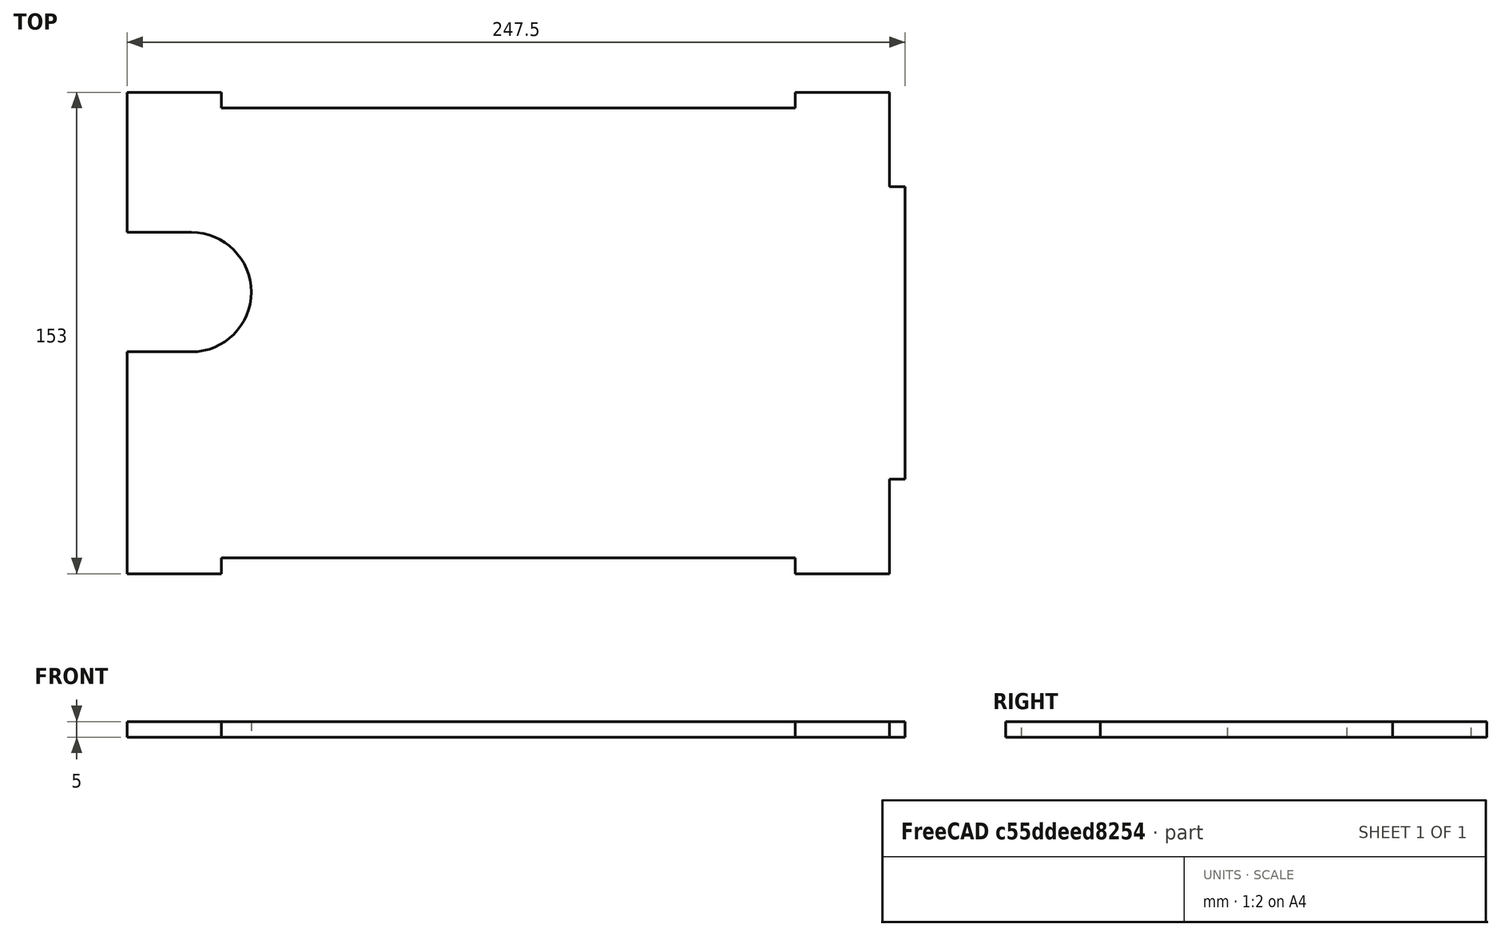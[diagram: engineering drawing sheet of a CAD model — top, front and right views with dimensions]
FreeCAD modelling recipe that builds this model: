
FCSTD DOCUMENT  (FreeCAD 0.15R4671 (Git))
Label: lower_side_axis_B
License: All rights reserved
LicenseURL: http://en.wikipedia.org/wiki/All_rights_reserved
objects: Sketcher::SketchObject×1, PartDesign::Pad×1
note: 3 computed .brp shape members not serialized (recipe doc carries the construction recipe); baked Part::Feature solids carry a one-line shape summary decoded from their .brp

FEATURE [Sketcher::SketchObject] Sketch
  sketch-geometry (20):
    g0: LineSegment StartX=121.25 StartY=46.5 StartZ=0 EndX=121.25 EndY=76.5 EndZ=0
    g1: LineSegment StartX=121.25 StartY=76.5 StartZ=0 EndX=91.25 EndY=76.5 EndZ=0
    g2: LineSegment StartX=91.25 StartY=76.5 StartZ=0 EndX=91.25 EndY=71.5 EndZ=0
    g3: LineSegment StartX=91.25 StartY=71.5 StartZ=0 EndX=-91.25 EndY=71.5 EndZ=0
    g4: LineSegment StartX=-91.25 StartY=71.5 StartZ=0 EndX=-91.25 EndY=76.5 EndZ=0
    g5: LineSegment StartX=-91.25 StartY=76.5 StartZ=0 EndX=-121.25 EndY=76.5 EndZ=0
    g6: LineSegment StartX=-121.25 StartY=76.5 StartZ=0 EndX=-121.25 EndY=32 EndZ=0
    g7: LineSegment StartX=-121.25 StartY=-6 StartZ=0 EndX=-121.25 EndY=-76.5 EndZ=0
    g8: LineSegment StartX=-121.25 StartY=-76.5 StartZ=0 EndX=-91.25 EndY=-76.5 EndZ=0
    g9: LineSegment StartX=-91.25 StartY=-76.5 StartZ=0 EndX=-91.25 EndY=-71.5 EndZ=0
    g10: LineSegment StartX=-91.25 StartY=-71.5 StartZ=0 EndX=91.25 EndY=-71.5 EndZ=0
    g11: LineSegment StartX=91.25 StartY=-71.5 StartZ=0 EndX=91.25 EndY=-76.5 EndZ=0
    g12: LineSegment StartX=91.25 StartY=-76.5 StartZ=0 EndX=121.25 EndY=-76.5 EndZ=0
    g13: LineSegment StartX=121.25 StartY=-76.5 StartZ=0 EndX=121.25 EndY=-46.5 EndZ=0
    g14: LineSegment StartX=121.25 StartY=-46.5 StartZ=0 EndX=126.25 EndY=-46.5 EndZ=0
    g15: LineSegment StartX=126.25 StartY=-46.5 StartZ=0 EndX=126.25 EndY=46.5 EndZ=0
    g16: LineSegment StartX=126.25 StartY=46.5 StartZ=0 EndX=121.25 EndY=46.5 EndZ=0
    g17: LineSegment StartX=-121.25 StartY=32 StartZ=0 EndX=-100.75 EndY=32 EndZ=0
    g18: ArcOfCircle CenterX=-100.75 CenterY=13 CenterZ=0 NormalX=0 NormalY=0 NormalZ=1 Radius=19 StartAngle=4.71239 EndAngle=7.85398
    g19: LineSegment StartX=-100.75 StartY=-6 StartZ=0 EndX=-121.25 EndY=-6 EndZ=0
  constraints (59):
    c: Coincident(g5,g6)
    c: Coincident(g4,g5)
    c: Coincident(g3,g4)
    c: Coincident(g2,g3)
    c: Coincident(g1,g2)
    c: Coincident(g0,g1)
    c: Coincident(g0,g16)
    c: Coincident(g15,g16)
    c: Coincident(g14,g15)
    c: Coincident(g13,g14)
    c: Coincident(g12,g13)
    c: Coincident(g11,g12)
    c: Coincident(g10,g11)
    c: Coincident(g9,g10)
    c: Coincident(g8,g9)
    c: Coincident(g7,g8)
    c: Vertical(g6)
    c: Vertical(g7)
    c: Vertical(g9)
    c: Vertical(g4)
    c: Vertical(g2)
    c: Vertical(g11)
    c: Vertical(g13)
    c: Vertical(g15)
    c: Vertical(g0)
    c: Horizontal(g5)
    c: Horizontal(g3)
    c: Horizontal(g1)
    c: Horizontal(g16)
    c: Horizontal(g14)
    c: Horizontal(g12)
    c: Horizontal(g10)
    c: Horizontal(g8)
    c: Equal(g4,g2)
    c: Equal(g2,g16)
    c: Equal(g16,g14)
    c: Equal(g14,g11)
    c: Equal(g11,g9)
    c: DistanceX(g16) = -5
    c: Equal(g5,g1)
    c: Equal(g1,g0)
    c: Equal(g0,g13)
    c: Equal(g13,g12)
    c: Equal(g12,g8)
    c: DistanceX(g1) = -30
    c: DistanceX(g5,g0) = 242.5
    c: DistanceY(g3,g9) = -143
    c: Coincident(g6,g17)
    c: Horizontal(g17)
    c: Tangent(g17,g18) = 1.5708
    c: Tangent(g18,g19) = 1.5708
    c: Horizontal(g19)
    c: Coincident(g7,g19)
    c: Radius(g18) = 19
    c: DistanceY(g18,g3) = 58.5
    c: DistanceX(g17,g3) = 9.5
    c: Equal(g17,g19)
    c: Symmetric(g8,g11,g-2)
    c: Symmetric(g15,g14,g-1)
FEATURE [PartDesign::Pad] Pad
  Length = 5
  Length2 = 100
  Sketch = -> Sketch
  Type = 0
